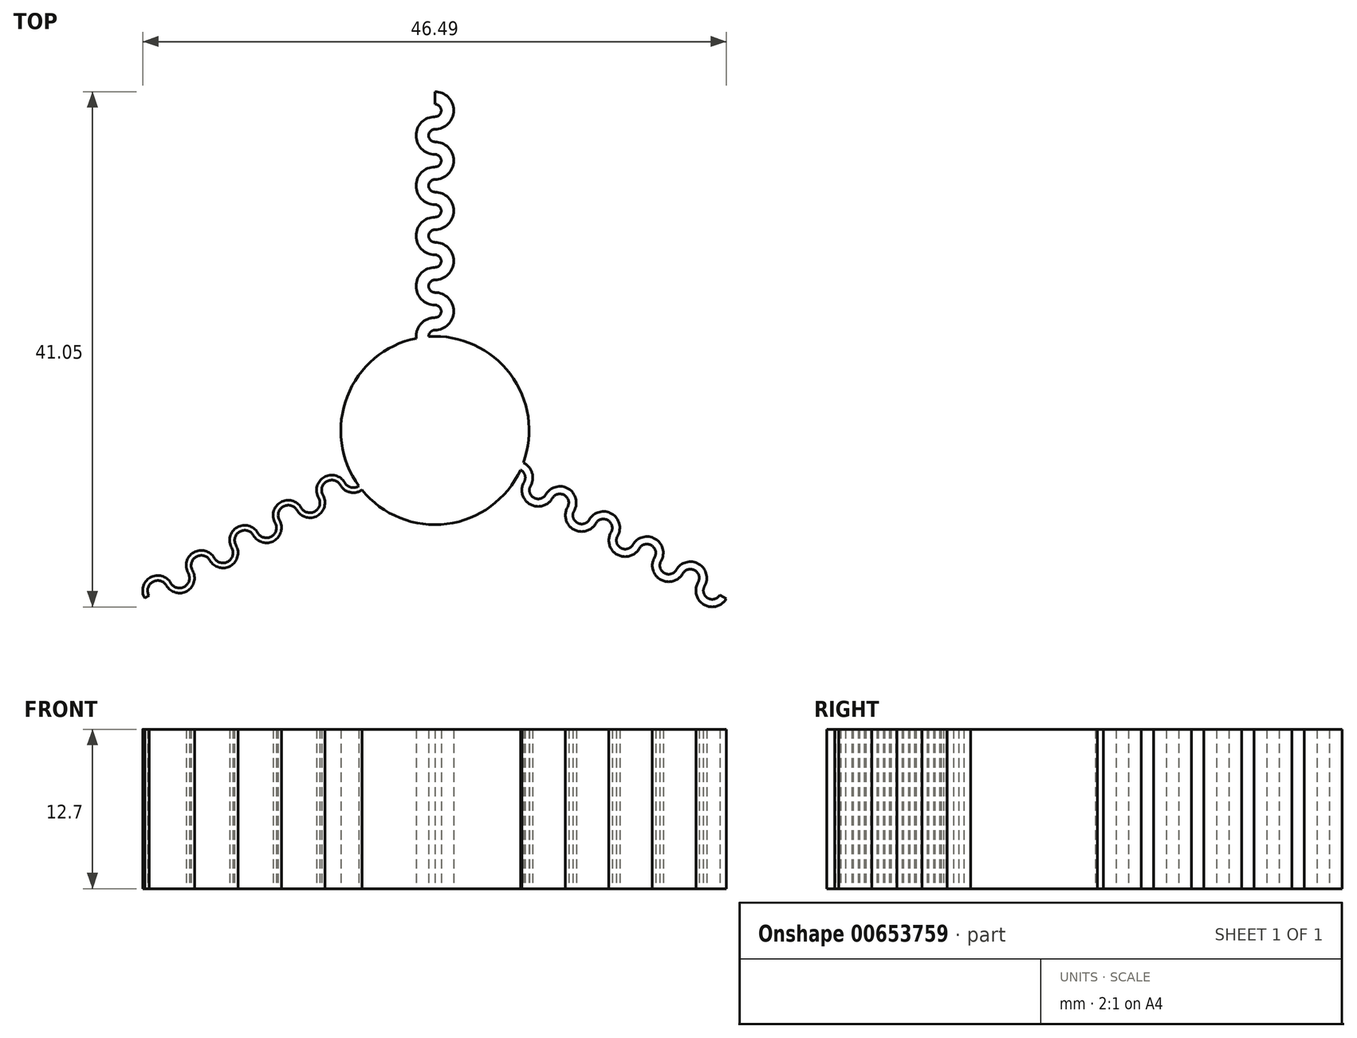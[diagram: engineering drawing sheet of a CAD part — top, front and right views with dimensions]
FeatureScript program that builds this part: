
annotation { "Feature Type Name" : "Feature", "Feature Type Description" : "" }
export const myFeature = defineFeature(function(context is Context, id is Id, definition is map)
    precondition{}
    {
        {
            var Q0;
            Q0=qCreatedBy(makeId("Top.planeOp"),FACE);
            var sketch = newSketch(context, id + "F0", { "sketchPlane" : qUnion([Q0])});
            skCircle(sketch, "E0", {"center": v(0, 0) * mm, "radius": 7.5 * mm});
            skLineSegment(sketch, "E1", {"start": v(0, 7.5) * mm, "end": v(0, 40.27) * mm, "construction": true});
            skLineSegment(sketch, "E2.bottom", {"start": v(1, 40.27) * mm, "end": v(-1, 40.27) * mm, "construction": true});
            skLineSegment(sketch, "E2.top", {"start": v(1, 7.5) * mm, "end": v(-1, 7.5) * mm, "construction": true});
            skLineSegment(sketch, "E2.left", {"start": v(1, 40.27) * mm, "end": v(1, 7.5) * mm, "construction": true});
            skLineSegment(sketch, "E2.right", {"start": v(-1, 40.27) * mm, "end": v(-1, 7.5) * mm, "construction": true});
            skPoint(sketch, "E2.middle", {"position": v(0, 23.88) * mm});
            skArc(sketch, "E3", {"start": v(0, 8.5) * mm, "mid": v(-1, 7.5) * mm, "end": v(0, 6.5) * mm, "construction": true});
            skArc(sketch, "E4", {"start": v(0, 8.5) * mm, "mid": v(1, 9.5) * mm, "end": v(0, 10.5) * mm, "construction": true});
            skArc(sketch, "E5.0.1.0", {"start": v(0, 12.5) * mm, "mid": v(-1, 11.5) * mm, "end": v(0, 10.5) * mm, "construction": true});
            skArc(sketch, "E5.0.1.1", {"start": v(0, 12.5) * mm, "mid": v(1, 13.5) * mm, "end": v(0, 14.5) * mm, "construction": true});
            skArc(sketch, "E5.0.2.0", {"start": v(0, 16.5) * mm, "mid": v(-1, 15.5) * mm, "end": v(0, 14.5) * mm, "construction": true});
            skArc(sketch, "E5.0.2.1", {"start": v(0, 16.5) * mm, "mid": v(1, 17.5) * mm, "end": v(0, 18.5) * mm, "construction": true});
            skArc(sketch, "E5.0.3.0", {"start": v(0, 20.5) * mm, "mid": v(-1, 19.5) * mm, "end": v(0, 18.5) * mm, "construction": true});
            skArc(sketch, "E5.0.3.1", {"start": v(0, 20.5) * mm, "mid": v(1, 21.5) * mm, "end": v(0, 22.5) * mm, "construction": true});
            skArc(sketch, "E5.0.4.0", {"start": v(0, 24.5) * mm, "mid": v(-1, 23.5) * mm, "end": v(0, 22.5) * mm, "construction": true});
            skArc(sketch, "E5.0.4.1", {"start": v(0, 24.5) * mm, "mid": v(1, 25.5) * mm, "end": v(0, 26.5) * mm, "construction": true});
            skLineSegment(sketch, "E5.direction1", {"start": v(0, 7.5) * mm, "end": v(-4.17, 7.5) * mm, "construction": true});
            skLineSegment(sketch, "E5.direction2", {"start": v(0, 7.5) * mm, "end": v(0, 11.5) * mm, "construction": true});
            skLineSegment(sketch, "E6", {"start": v(0, 7.5) * mm, "end": v(0, 5.46) * mm, "construction": true});
            skArc(sketch, "E7.0", {"start": v(0, 9) * mm, "mid": v(-1.5, 7.5) * mm, "end": v(0, 6) * mm});
            skArc(sketch, "E7.1", {"start": v(0, 9) * mm, "mid": v(0.5, 9.5) * mm, "end": v(0, 10) * mm});
            skArc(sketch, "E7.2", {"start": v(0, 13) * mm, "mid": v(-1.5, 11.5) * mm, "end": v(0, 10) * mm});
            skArc(sketch, "E7.3", {"start": v(0, 13) * mm, "mid": v(0.5, 13.5) * mm, "end": v(0, 14) * mm});
            skArc(sketch, "E7.4", {"start": v(0, 17) * mm, "mid": v(-1.5, 15.5) * mm, "end": v(0, 14) * mm});
            skArc(sketch, "E7.5", {"start": v(0, 17) * mm, "mid": v(0.5, 17.5) * mm, "end": v(0, 18) * mm});
            skArc(sketch, "E7.6", {"start": v(0, 25) * mm, "mid": v(0.5, 25.5) * mm, "end": v(0, 26) * mm});
            skArc(sketch, "E7.7", {"start": v(0, 25) * mm, "mid": v(-1.5, 23.5) * mm, "end": v(0, 22) * mm});
            skArc(sketch, "E7.8", {"start": v(0, 21) * mm, "mid": v(0.5, 21.5) * mm, "end": v(0, 22) * mm});
            skArc(sketch, "E7.9", {"start": v(0, 21) * mm, "mid": v(-1.5, 19.5) * mm, "end": v(0, 18) * mm});
            skArc(sketch, "E8.0", {"start": v(0, 8) * mm, "mid": v(-0.5, 7.5) * mm, "end": v(0, 7) * mm});
            skArc(sketch, "E8.1", {"start": v(0, 8) * mm, "mid": v(1.5, 9.5) * mm, "end": v(0, 11) * mm});
            skArc(sketch, "E8.2", {"start": v(0, 12) * mm, "mid": v(-0.5, 11.5) * mm, "end": v(0, 11) * mm});
            skArc(sketch, "E8.3", {"start": v(0, 12) * mm, "mid": v(1.5, 13.5) * mm, "end": v(0, 15) * mm});
            skArc(sketch, "E8.4", {"start": v(0, 16) * mm, "mid": v(-0.5, 15.5) * mm, "end": v(0, 15) * mm});
            skArc(sketch, "E8.5", {"start": v(0, 16) * mm, "mid": v(1.5, 17.5) * mm, "end": v(0, 19) * mm});
            skArc(sketch, "E8.6", {"start": v(0, 24) * mm, "mid": v(1.5, 25.5) * mm, "end": v(0, 27) * mm});
            skArc(sketch, "E8.7", {"start": v(0, 24) * mm, "mid": v(-0.5, 23.5) * mm, "end": v(0, 23) * mm});
            skArc(sketch, "E8.8", {"start": v(0, 20) * mm, "mid": v(1.5, 21.5) * mm, "end": v(0, 23) * mm});
            skArc(sketch, "E8.9", {"start": v(0, 20) * mm, "mid": v(-0.5, 19.5) * mm, "end": v(0, 19) * mm});
            skArc(sketch, "E9.1.0", {"start": v(-7.36, -4.25) * mm, "mid": v(-6, -4.62) * mm, "end": v(-5.63, -3.25) * mm, "construction": true});
            skArc(sketch, "E9.1.1", {"start": v(-7.36, -4.25) * mm, "mid": v(-8.73, -3.88) * mm, "end": v(-9.1, -5.25) * mm, "construction": true});
            skArc(sketch, "E9.1.2", {"start": v(-10.83, -6.25) * mm, "mid": v(-9.46, -6.62) * mm, "end": v(-9.1, -5.25) * mm, "construction": true});
            skArc(sketch, "E9.1.3", {"start": v(-10.83, -6.25) * mm, "mid": v(-12.2, -5.88) * mm, "end": v(-12.56, -7.25) * mm, "construction": true});
            skArc(sketch, "E9.1.4", {"start": v(-14.29, -8.25) * mm, "mid": v(-12.92, -8.62) * mm, "end": v(-12.56, -7.25) * mm, "construction": true});
            skArc(sketch, "E9.1.5", {"start": v(-14.29, -8.25) * mm, "mid": v(-15.66, -7.88) * mm, "end": v(-16.02, -9.25) * mm, "construction": true});
            skArc(sketch, "E9.1.6", {"start": v(-17.75, -10.25) * mm, "mid": v(-16.39, -10.62) * mm, "end": v(-16.02, -9.25) * mm, "construction": true});
            skArc(sketch, "E9.1.7", {"start": v(-17.75, -10.25) * mm, "mid": v(-19.12, -9.88) * mm, "end": v(-19.49, -11.25) * mm, "construction": true});
            skArc(sketch, "E9.1.8", {"start": v(-21.22, -12.25) * mm, "mid": v(-19.85, -12.62) * mm, "end": v(-19.49, -11.25) * mm, "construction": true});
            skArc(sketch, "E9.1.9", {"start": v(-21.22, -12.25) * mm, "mid": v(-22.58, -11.88) * mm, "end": v(-22.95, -13.25) * mm, "construction": true});
            skArc(sketch, "E9.2.0", {"start": v(7.36, -4.25) * mm, "mid": v(7, -2.88) * mm, "end": v(5.63, -3.25) * mm, "construction": true});
            skArc(sketch, "E9.2.1", {"start": v(7.36, -4.25) * mm, "mid": v(7.73, -5.62) * mm, "end": v(9.1, -5.25) * mm, "construction": true});
            skArc(sketch, "E9.2.2", {"start": v(10.83, -6.25) * mm, "mid": v(10.46, -4.88) * mm, "end": v(9.1, -5.25) * mm, "construction": true});
            skArc(sketch, "E9.2.3", {"start": v(10.83, -6.25) * mm, "mid": v(11.2, -7.62) * mm, "end": v(12.56, -7.25) * mm, "construction": true});
            skArc(sketch, "E9.2.4", {"start": v(14.29, -8.25) * mm, "mid": v(13.92, -6.88) * mm, "end": v(12.56, -7.25) * mm, "construction": true});
            skArc(sketch, "E9.2.5", {"start": v(14.29, -8.25) * mm, "mid": v(14.66, -9.62) * mm, "end": v(16.02, -9.25) * mm, "construction": true});
            skArc(sketch, "E9.2.6", {"start": v(17.75, -10.25) * mm, "mid": v(17.39, -8.88) * mm, "end": v(16.02, -9.25) * mm, "construction": true});
            skArc(sketch, "E9.2.7", {"start": v(17.75, -10.25) * mm, "mid": v(18.12, -11.62) * mm, "end": v(19.49, -11.25) * mm, "construction": true});
            skArc(sketch, "E9.2.8", {"start": v(21.22, -12.25) * mm, "mid": v(20.85, -10.88) * mm, "end": v(19.49, -11.25) * mm, "construction": true});
            skArc(sketch, "E9.2.9", {"start": v(21.22, -12.25) * mm, "mid": v(21.58, -13.62) * mm, "end": v(22.95, -13.25) * mm, "construction": true});
            skArc(sketch, "E10.0", {"start": v(7.62, -4.4) * mm, "mid": v(7.15, -2.62) * mm, "end": v(5.37, -3.1) * mm});
            skArc(sketch, "E10.1", {"start": v(7.62, -4.4) * mm, "mid": v(7.88, -5.36) * mm, "end": v(8.83, -5.1) * mm});
            skArc(sketch, "E10.2", {"start": v(11.09, -6.4) * mm, "mid": v(10.6, -4.62) * mm, "end": v(8.83, -5.1) * mm});
            skArc(sketch, "E10.3", {"start": v(11.09, -6.4) * mm, "mid": v(11.34, -7.36) * mm, "end": v(12.3, -7.1) * mm});
            skArc(sketch, "E10.4", {"start": v(14.55, -8.4) * mm, "mid": v(14.07, -6.62) * mm, "end": v(12.3, -7.1) * mm});
            skArc(sketch, "E10.5", {"start": v(14.55, -8.4) * mm, "mid": v(14.8, -9.36) * mm, "end": v(15.76, -9.1) * mm});
            skArc(sketch, "E10.6", {"start": v(21.48, -12.4) * mm, "mid": v(21.73, -13.36) * mm, "end": v(22.69, -13.1) * mm});
            skArc(sketch, "E10.7", {"start": v(21.48, -12.4) * mm, "mid": v(21, -10.62) * mm, "end": v(19.23, -11.1) * mm});
            skArc(sketch, "E10.8", {"start": v(18.01, -10.4) * mm, "mid": v(18.27, -11.36) * mm, "end": v(19.23, -11.1) * mm});
            skArc(sketch, "E10.9", {"start": v(18.01, -10.4) * mm, "mid": v(17.54, -8.62) * mm, "end": v(15.76, -9.1) * mm});
            skArc(sketch, "E11.0", {"start": v(7.1, -4.1) * mm, "mid": v(6.85, -3.14) * mm, "end": v(5.89, -3.4) * mm});
            skArc(sketch, "E11.1", {"start": v(7.1, -4.1) * mm, "mid": v(7.58, -5.88) * mm, "end": v(9.35, -5.4) * mm});
            skArc(sketch, "E11.2", {"start": v(10.57, -6.1) * mm, "mid": v(10.3, -5.14) * mm, "end": v(9.35, -5.4) * mm});
            skArc(sketch, "E11.3", {"start": v(10.57, -6.1) * mm, "mid": v(11.04, -7.88) * mm, "end": v(12.82, -7.4) * mm});
            skArc(sketch, "E11.4", {"start": v(14.03, -8.1) * mm, "mid": v(13.77, -7.14) * mm, "end": v(12.82, -7.4) * mm});
            skArc(sketch, "E11.5", {"start": v(14.03, -8.1) * mm, "mid": v(14.5, -9.88) * mm, "end": v(16.28, -9.4) * mm});
            skArc(sketch, "E11.6", {"start": v(20.96, -12.1) * mm, "mid": v(21.43, -13.88) * mm, "end": v(23.2, -13.4) * mm});
            skArc(sketch, "E11.7", {"start": v(20.96, -12.1) * mm, "mid": v(20.7, -11.14) * mm, "end": v(19.75, -11.4) * mm});
            skArc(sketch, "E11.8", {"start": v(17.5, -10.1) * mm, "mid": v(17.97, -11.88) * mm, "end": v(19.75, -11.4) * mm});
            skArc(sketch, "E11.9", {"start": v(17.5, -10.1) * mm, "mid": v(17.24, -9.14) * mm, "end": v(16.28, -9.4) * mm});
            skLineSegment(sketch, "E12", {"start": v(0, 27) * mm, "end": v(0, 26) * mm});
            skLineSegment(sketch, "E13", {"start": v(22.69, -13.1) * mm, "end": v(23.2, -13.4) * mm});
            skArc(sketch, "E14.0", {"start": v(-7.53, -4.35) * mm, "mid": v(-5.9, -4.79) * mm, "end": v(-5.46, -3.15) * mm});
            skArc(sketch, "E14.1", {"start": v(-7.53, -4.35) * mm, "mid": v(-8.63, -4.06) * mm, "end": v(-8.92, -5.15) * mm});
            skArc(sketch, "E14.2", {"start": v(-11, -6.35) * mm, "mid": v(-9.36, -6.79) * mm, "end": v(-8.92, -5.15) * mm});
            skArc(sketch, "E14.3", {"start": v(-11, -6.35) * mm, "mid": v(-12.1, -6.06) * mm, "end": v(-12.38, -7.15) * mm});
            skArc(sketch, "E14.4", {"start": v(-14.46, -8.35) * mm, "mid": v(-12.82, -8.79) * mm, "end": v(-12.38, -7.15) * mm});
            skArc(sketch, "E14.5", {"start": v(-14.46, -8.35) * mm, "mid": v(-15.56, -8.06) * mm, "end": v(-15.85, -9.15) * mm});
            skArc(sketch, "E14.6", {"start": v(-21.4, -12.35) * mm, "mid": v(-22.48, -12.06) * mm, "end": v(-22.78, -13.15) * mm});
            skArc(sketch, "E14.7", {"start": v(-21.4, -12.35) * mm, "mid": v(-19.75, -12.79) * mm, "end": v(-19.31, -11.15) * mm});
            skArc(sketch, "E14.8", {"start": v(-17.93, -10.35) * mm, "mid": v(-19.02, -10.06) * mm, "end": v(-19.31, -11.15) * mm});
            skArc(sketch, "E14.9", {"start": v(-17.93, -10.35) * mm, "mid": v(-16.29, -10.79) * mm, "end": v(-15.85, -9.15) * mm});
            skArc(sketch, "E15.0", {"start": v(-7.19, -4.15) * mm, "mid": v(-6.1, -4.44) * mm, "end": v(-5.8, -3.35) * mm});
            skArc(sketch, "E15.1", {"start": v(-7.19, -4.15) * mm, "mid": v(-8.83, -3.71) * mm, "end": v(-9.27, -5.35) * mm});
            skArc(sketch, "E15.2", {"start": v(-10.65, -6.15) * mm, "mid": v(-9.56, -6.44) * mm, "end": v(-9.27, -5.35) * mm});
            skArc(sketch, "E15.3", {"start": v(-10.65, -6.15) * mm, "mid": v(-12.3, -5.71) * mm, "end": v(-12.73, -7.35) * mm});
            skArc(sketch, "E15.4", {"start": v(-14.12, -8.15) * mm, "mid": v(-13.02, -8.44) * mm, "end": v(-12.73, -7.35) * mm});
            skArc(sketch, "E15.5", {"start": v(-14.12, -8.15) * mm, "mid": v(-15.76, -7.71) * mm, "end": v(-16.2, -9.35) * mm});
            skArc(sketch, "E15.6", {"start": v(-21.04, -12.15) * mm, "mid": v(-22.68, -11.71) * mm, "end": v(-23.12, -13.35) * mm});
            skArc(sketch, "E15.7", {"start": v(-21.04, -12.15) * mm, "mid": v(-19.95, -12.44) * mm, "end": v(-19.66, -11.35) * mm});
            skArc(sketch, "E15.8", {"start": v(-17.58, -10.15) * mm, "mid": v(-19.22, -9.71) * mm, "end": v(-19.66, -11.35) * mm});
            skArc(sketch, "E15.9", {"start": v(-17.58, -10.15) * mm, "mid": v(-16.49, -10.44) * mm, "end": v(-16.2, -9.35) * mm});
            skLineSegment(sketch, "E16", {"start": v(-22.78, -13.15) * mm, "end": v(-23.12, -13.35) * mm});
            skSolve(sketch);
        }
        {
            var Q0;
            Q0 = qSketchRegion(id + "F0", true);
            extrude(context, id + "F1", {"entities" : qUnion([Q0]), "depth" : 12.7 * mm, "offsetDistance" : 25.4 * mm});
        }
    });
